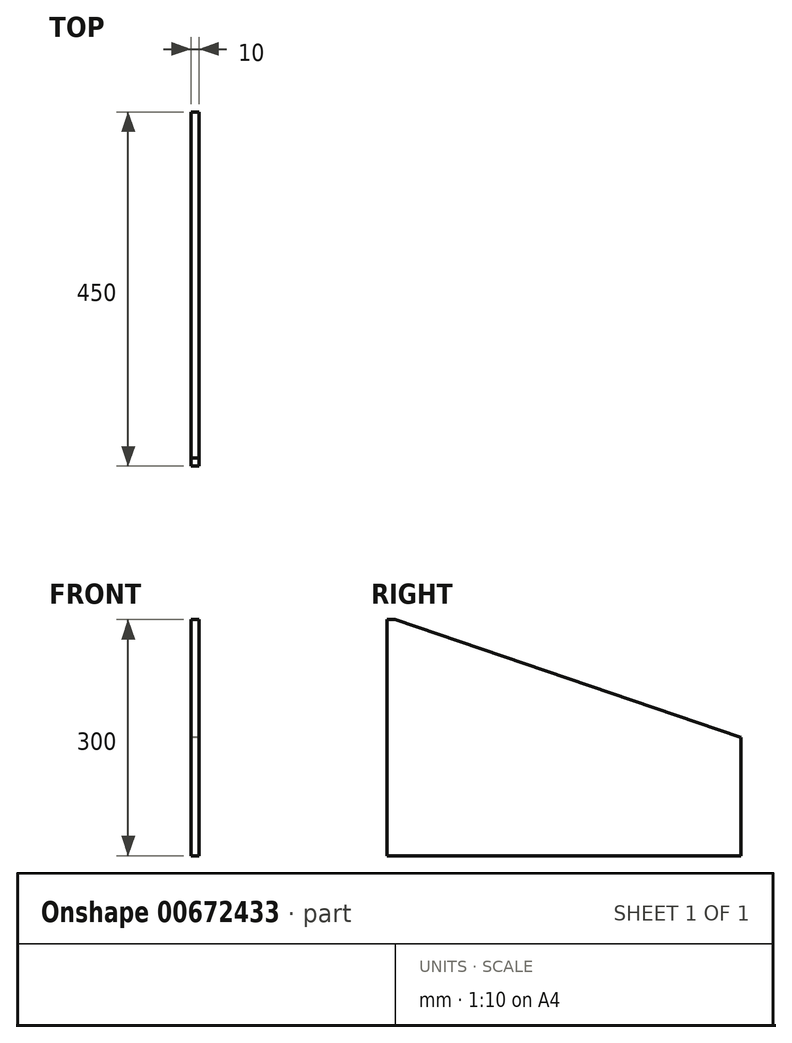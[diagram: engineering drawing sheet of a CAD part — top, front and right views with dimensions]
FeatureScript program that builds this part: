
annotation { "Feature Type Name" : "Feature", "Feature Type Description" : "" }
export const myFeature = defineFeature(function(context is Context, id is Id, definition is map)
    precondition{}
    {
        {
            var Q0;
            Q0=qCreatedBy(makeId("Right.planeOp"),FACE);
            var sketch = newSketch(context, id + "F0", { "sketchPlane" : qUnion([Q0])});
            skLineSegment(sketch, "E0.bottom", {"start": v(-143.9, 0) * mm, "end": v(-133.9, 0) * mm});
            skLineSegment(sketch, "E0.top", {"start": v(-143.9, 300) * mm, "end": v(-133.9, 300) * mm});
            skLineSegment(sketch, "E0.left", {"start": v(-143.9, 0) * mm, "end": v(-143.9, 300) * mm});
            skLineSegment(sketch, "E0.right", {"start": v(-133.9, 0) * mm, "end": v(-133.9, 300) * mm});
            skLineSegment(sketch, "E1.bottom", {"start": v(306.1, 0) * mm, "end": v(117.53, 0) * mm});
            skLineSegment(sketch, "E1.top", {"start": v(306.1, 150) * mm, "end": v(117.53, 150) * mm});
            skLineSegment(sketch, "E1.left", {"start": v(306.1, 0) * mm, "end": v(306.1, 150) * mm});
            skLineSegment(sketch, "E1.right", {"start": v(117.53, 0) * mm, "end": v(117.53, 150) * mm});
            skLineSegment(sketch, "E2", {"start": v(-133.9, 300) * mm, "end": v(306.1, 150) * mm});
            skLineSegment(sketch, "E3", {"start": v(-133.9, 0) * mm, "end": v(117.53, 0) * mm});
            skSolve(sketch);
        }
        {
            var Q0;
            Q0 = qSketchRegion(id + "F0", true);
            extrude(context, id + "F1", {"entities" : qUnion([Q0]), "depth" : 10 * mm, "offsetDistance" : 25 * mm});
        }
    });
